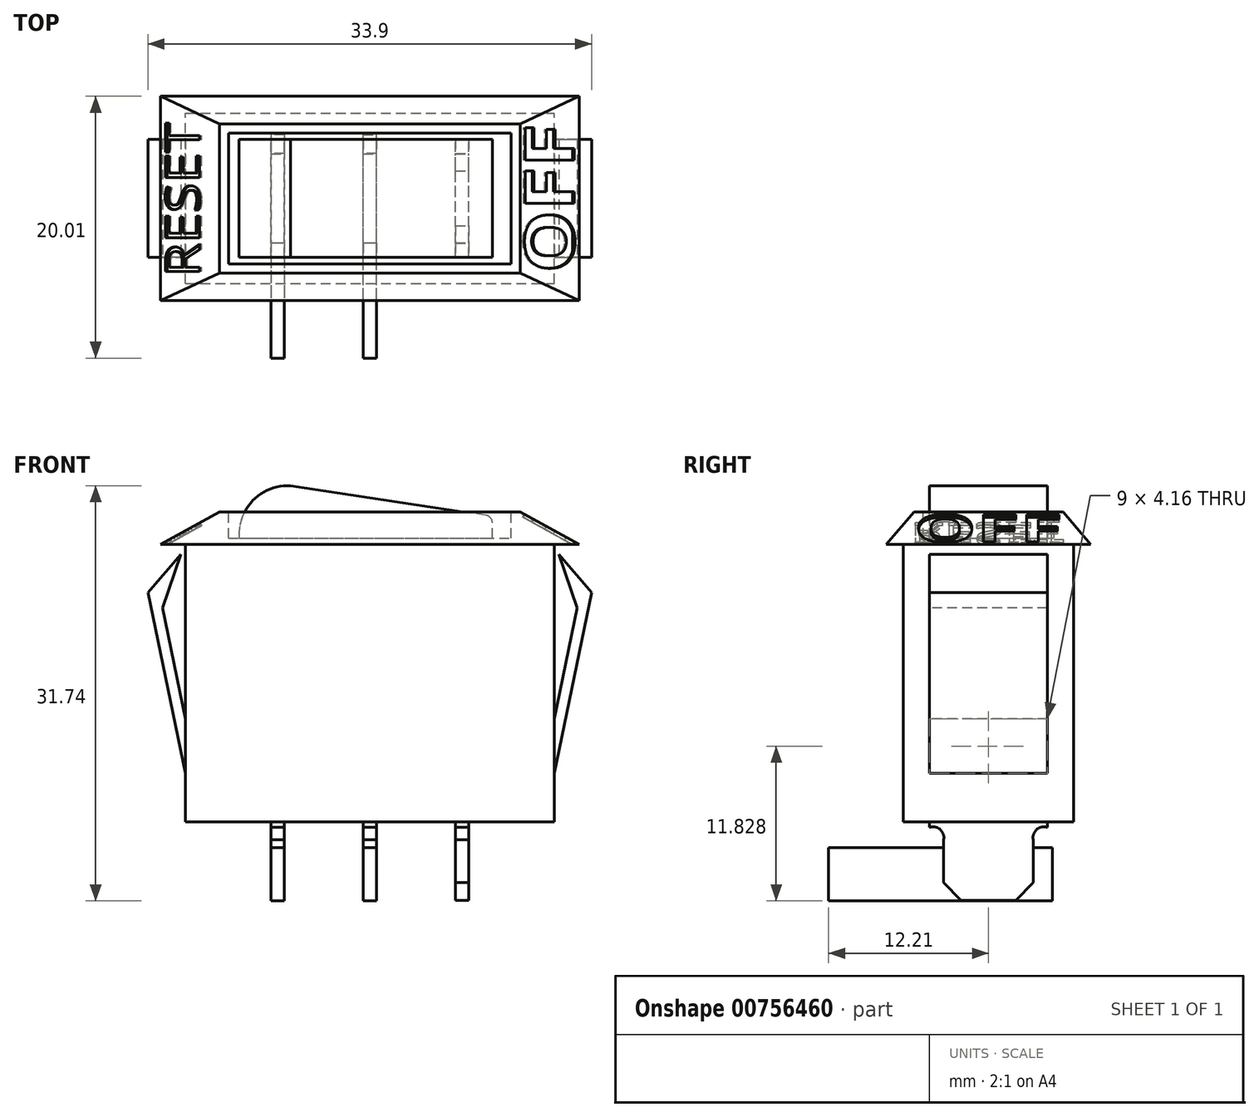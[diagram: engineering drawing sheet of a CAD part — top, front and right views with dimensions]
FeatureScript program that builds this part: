
annotation { "Feature Type Name" : "Feature", "Feature Type Description" : "" }
export const myFeature = defineFeature(function(context is Context, id is Id, definition is map)
    precondition{}
    {
        {
            var Q0;
            Q0=qCreatedBy(makeId("Front.planeOp"),FACE);
            var sketch = newSketch(context, id + "F0", { "sketchPlane" : qUnion([Q0])});
            skLineSegment(sketch, "E0.bottom", {"start": v(-14.1, -10.6) * mm, "end": v(14.1, -10.6) * mm});
            skLineSegment(sketch, "E0.top", {"start": v(-14.1, 10.6) * mm, "end": v(14.1, 10.6) * mm});
            skLineSegment(sketch, "E0.left", {"start": v(-14.1, -10.6) * mm, "end": v(-14.1, 10.6) * mm});
            skLineSegment(sketch, "E0.right", {"start": v(14.1, -10.6) * mm, "end": v(14.1, 10.6) * mm});
            skPoint(sketch, "E0.middle", {"position": v(0, 0) * mm});
            skSolve(sketch);
        }
        {
            var Q0;
            Q0=makeQuery(id+"F0.imprint","IMPRINT",FACE,{"disambiguationData":[TD([[makeQuery(id+"F0.imprint","IMPRINT",EDGE,{"derivedFrom":sQuery(id+"F0.wireOp",EDGE,"E0.bottom")}),1.0]])]});
            extrude(context, id + "F1", {"entities" : qUnion([Q0]), "depth" : 13 * mm, "offsetDistance" : 25 * mm, "symmetric" : true});
        }
        {
            var Q0;
            Q0=makeQuery(id+"F1.opExtrude","SWEPT_FACE",FACE,{"disambiguationData":[OSD([sQuery(id+"F0.wireOp",EDGE,"E0.top")])]});
            var sketch = newSketch(context, id + "F2", { "sketchPlane" : qUnion([Q0])});
            skLineSegment(sketch, "E1.bottom", {"start": v(-16, -7.8) * mm, "end": v(16, -7.8) * mm});
            skLineSegment(sketch, "E1.top", {"start": v(-16, 7.8) * mm, "end": v(16, 7.8) * mm});
            skLineSegment(sketch, "E1.left", {"start": v(-16, -7.8) * mm, "end": v(-16, 7.8) * mm});
            skLineSegment(sketch, "E1.right", {"start": v(16, -7.8) * mm, "end": v(16, 7.8) * mm});
            skPoint(sketch, "E1.middle", {"position": v(0, 0) * mm});
            skSolve(sketch);
        }
        {
            var Q0;
            Q0=makeQuery(id+"F2.imprint","IMPRINT",FACE,{"disambiguationData":[TD([[makeQuery(id+"F2.imprint","IMPRINT",EDGE,{"derivedFrom":sQuery(id+"F2.wireOp",EDGE,"E1.bottom")}),1.0]])]});
            var Q1;
            {var subQ0=sQuery(id+"F0.wireOp",EDGE,"E0.top");Q1=makeQuery(id+"F2.imprint","IMPRINT",FACE,{"disambiguationData":[TD([[makeQuery(id+"F2.imprint","IMPRINT",EDGE,{"derivedFrom":makeQuery(id+"F1.opExtrude","CAP_EDGE",EDGE,{"disambiguationData":[OSD([subQ0])],"isStart":true})}),-1.0]])]});}
            extrude(context, id + "F3", {"entities" : qUnion([Q0, Q1]), "operationType" : NewBodyOperationType.ADD, "depth" : 2.5 * mm, "offsetDistance" : 25 * mm});
        }
        {
            var Q0;
            Q0=makeQuery(id+"F3.opExtrude","CAP_FACE",FACE,{"disambiguationData":[OSD([sQuery(id+"F2.wireOp",EDGE,"E1.bottom"),sQuery(id+"F2.wireOp",EDGE,"E1.top"),sQuery(id+"F2.wireOp",EDGE,"E1.left"),sQuery(id+"F2.wireOp",EDGE,"E1.right")])],"isStart":false});
            var sketch = newSketch(context, id + "F4", { "sketchPlane" : qUnion([Q0])});
            skLineSegment(sketch, "E2.bottom", {"start": v(-10.8, -5) * mm, "end": v(10.8, -5) * mm});
            skLineSegment(sketch, "E2.top", {"start": v(-10.8, 5) * mm, "end": v(10.8, 5) * mm});
            skLineSegment(sketch, "E2.left", {"start": v(-10.8, -5) * mm, "end": v(-10.8, 5) * mm});
            skLineSegment(sketch, "E2.right", {"start": v(10.8, -5) * mm, "end": v(10.8, 5) * mm});
            skPoint(sketch, "E2.middle", {"position": v(0, 0) * mm});
            skSolve(sketch);
        }
        {
            var Q0;
            Q0=makeQuery(id+"F4.imprint","IMPRINT",FACE,{"disambiguationData":[TD([[makeQuery(id+"F4.imprint","IMPRINT",EDGE,{"derivedFrom":sQuery(id+"F4.wireOp",EDGE,"E2.bottom")}),1.0]])]});
            extrude(context, id + "F5", {"entities" : qUnion([Q0]), "operationType" : NewBodyOperationType.REMOVE, "oppositeDirection" : true, "depth" : 2 * mm, "offsetDistance" : 25 * mm});
        }
        {
            var Q0;
            Q0=makeQuery(id+"F5.boolean.opBoolean","COPY",FACE,{"derivedFrom":makeQuery(id+"F5.opExtrude","SWEPT_FACE",FACE,{"disambiguationData":[OSD([sQuery(id+"F4.wireOp",EDGE,"E2.top")])]})});
            cPlane(context, id + "F6", {"entities" : qUnion([Q0]), "cplaneType" : CPlaneType.OFFSET, "offset" : .5 * mm, "width" : 150 * mm, "height" : 150 * mm});
        }
        {
            var Q0;
            Q0=qCreatedBy(id+"F6.planeOp",FACE);
            var sketch = newSketch(context, id + "F7", { "sketchPlane" : qUnion([Q0])});
            skLineSegment(sketch, "E3.0", {"start": v(-10.8, 11.1) * mm, "end": v(10.8, 11.1) * mm});
            skLineSegment(sketch, "E4", {"start": v(-6.06, 11.1) * mm, "end": v(-6.06, 15.1) * mm, "construction": true});
            skArc(sketch, "E5", {"start": v(-6.06, 15.1) * mm, "mid": v(-8.92, 13.98) * mm, "end": v(-10, 11.1) * mm});
            skLineSegment(sketch, "E6", {"start": v(9.36, 11.1) * mm, "end": v(9.36, 12.27) * mm});
            skLineSegment(sketch, "E7", {"start": v(8.88, 12.83) * mm, "end": v(-6.06, 15.1) * mm});
            skPoint(sketch, "E8.visualSharp", {"position": v(9.36, 12.76) * mm});
            skArc(sketch, "E8.filletArc", {"start": v(9.36, 12.27) * mm, "mid": v(9.23, 12.64) * mm, "end": v(8.88, 12.83) * mm});
            skSolve(sketch);
        }
        {
            var Q0;
            {var subQ1=sQuery(id+"F7.wireOp",EDGE,"E5");Q0=makeQuery(id+"F7.imprint","IMPRINT",FACE,{"disambiguationData":[TD([[makeQuery(id+"F7.imprint","IMPRINT",EDGE,{"derivedFrom":subQ1}),1.0]])]});}
            extrude(context, id + "F8", {"entities" : qUnion([Q0]), "operationType" : NewBodyOperationType.ADD, "depth" : 9 * mm, "offsetDistance" : 25 * mm});
        }
        {
            var Q0;
            Q0=makeQuery(id+"F3.opExtrude","SWEPT_FACE",FACE,{"disambiguationData":[OSD([sQuery(id+"F2.wireOp",EDGE,"E1.right")])]});
            var sketch = newSketch(context, id + "F9", { "sketchPlane" : qUnion([Q0])});
            skLineSegment(sketch, "E9.0", {"start": v(-7.8, 13.1) * mm, "end": v(-7.8, 10.6) * mm});
            skLineSegment(sketch, "E9.1", {"start": v(-7.8, 13.1) * mm, "end": v(7.8, 13.1) * mm});
            skLineSegment(sketch, "E9.2", {"start": v(7.8, 13.1) * mm, "end": v(7.8, 10.6) * mm});
            skLineSegment(sketch, "E10", {"start": v(-7.8, 10.6) * mm, "end": v(-5.7, 13.1) * mm});
            skLineSegment(sketch, "E11.0", {"start": v(-5, 11.1) * mm, "end": v(-5, 13.1) * mm, "construction": true});
            skLineSegment(sketch, "E12", {"start": v(0, 10.6) * mm, "end": v(0, 13.1) * mm, "construction": true});
            skLineSegment(sketch, "E13.MirrorCS", {"start": v(7.8, 10.6) * mm, "end": v(5.7, 13.1) * mm});
            skSolve(sketch);
        }
        {
            var Q0;
            {var subQ0=sQuery(id+"F9.wireOp",EDGE,"E9.0");Q0=makeQuery(id+"F9.imprint","IMPRINT",FACE,{"disambiguationData":[TD([[makeQuery(id+"F9.imprint","IMPRINT",EDGE,{"derivedFrom":subQ0}),1.0]])]});}
            var Q1;
            {var subQ0=sQuery(id+"F9.wireOp",EDGE,"E9.2");Q1=makeQuery(id+"F9.imprint","IMPRINT",FACE,{"disambiguationData":[TD([[makeQuery(id+"F9.imprint","IMPRINT",EDGE,{"derivedFrom":subQ0}),-1.0]])]});}
            extrude(context, id + "F10", {"entities" : qUnion([Q0, Q1]), "operationType" : NewBodyOperationType.REMOVE, "endBound" : BoundingType.THROUGH_ALL, "oppositeDirection" : true, "depth" : 25 * mm, "offsetDistance" : 25 * mm});
        }
        {
            var Q0;
            Q0=makeQuery(id+"F1.opExtrude","CAP_FACE",FACE,{"disambiguationData":[OSD([sQuery(id+"F0.wireOp",EDGE,"E0.bottom"),sQuery(id+"F0.wireOp",EDGE,"E0.top"),sQuery(id+"F0.wireOp",EDGE,"E0.left"),sQuery(id+"F0.wireOp",EDGE,"E0.right")])],"isStart":false});
            cPlane(context, id + "F11", {"entities" : qUnion([Q0]), "cplaneType" : CPlaneType.OFFSET, "offset" : 1.3 * mm, "width" : 150 * mm, "height" : 150 * mm});
        }
        {
            var Q0;
            Q0=qCreatedBy(id+"F11.planeOp",FACE);
            var sketch = newSketch(context, id + "F12", { "sketchPlane" : qUnion([Q0])});
            skLineSegment(sketch, "E14.0", {"start": v(-16, 13.1) * mm, "end": v(-16, 10.6) * mm});
            skLineSegment(sketch, "E14.1", {"start": v(-16, 13.1) * mm, "end": v(16, 13.1) * mm});
            skLineSegment(sketch, "E14.2", {"start": v(16, 10.6) * mm, "end": v(16, 13.1) * mm});
            skLineSegment(sketch, "E15.0", {"start": v(-10.8, 11.1) * mm, "end": v(-10.8, 13.1) * mm, "construction": true});
            skLineSegment(sketch, "E16", {"start": v(0, 13.1) * mm, "end": v(0, 10.69) * mm, "construction": true});
            skLineSegment(sketch, "E17", {"start": v(-16, 10.6) * mm, "end": v(-11.5, 13.1) * mm});
            skLineSegment(sketch, "E18.MirrorCS", {"start": v(16, 10.6) * mm, "end": v(11.5, 13.1) * mm});
            skSolve(sketch);
        }
        {
            var Q0;
            {var subQ0=sQuery(id+"F12.wireOp",EDGE,"E14.0");Q0=makeQuery(id+"F12.imprint","IMPRINT",FACE,{"disambiguationData":[TD([[makeQuery(id+"F12.imprint","IMPRINT",EDGE,{"derivedFrom":subQ0}),1.0]])]});}
            var Q1;
            {var subQ0=sQuery(id+"F12.wireOp",EDGE,"E14.2");Q1=makeQuery(id+"F12.imprint","IMPRINT",FACE,{"disambiguationData":[TD([[makeQuery(id+"F12.imprint","IMPRINT",EDGE,{"derivedFrom":subQ0}),1.0]])]});}
            extrude(context, id + "F13", {"entities" : qUnion([Q0, Q1]), "operationType" : NewBodyOperationType.REMOVE, "endBound" : BoundingType.THROUGH_ALL, "oppositeDirection" : true, "depth" : 25 * mm, "offsetDistance" : 25 * mm});
        }
        {
            var Q0;
            Q0=makeQuery(id+"F1.opExtrude","CAP_FACE",FACE,{"disambiguationData":[OSD([sQuery(id+"F0.wireOp",EDGE,"E0.bottom"),sQuery(id+"F0.wireOp",EDGE,"E0.top"),sQuery(id+"F0.wireOp",EDGE,"E0.left"),sQuery(id+"F0.wireOp",EDGE,"E0.right")])],"isStart":false});
            cPlane(context, id + "F14", {"entities" : qUnion([Q0]), "cplaneType" : CPlaneType.OFFSET, "offset" : 2 * mm, "oppositeDirection" : true, "width" : 150 * mm, "height" : 150 * mm});
        }
        {
            var Q0;
            Q0=qCreatedBy(id+"F14.planeOp",FACE);
            var sketch = newSketch(context, id + "F15", { "sketchPlane" : qUnion([Q0])});
            skLineSegment(sketch, "E19.0", {"start": v(-14.1, -10.6) * mm, "end": v(-14.1, 10.6) * mm});
            skLineSegment(sketch, "E19.1", {"start": v(14.1, -10.6) * mm, "end": v(14.1, 10.6) * mm});
            skLineSegment(sketch, "E20", {"start": v(-14.1, -6.9) * mm, "end": v(-16.95, 6.94) * mm});
            skLineSegment(sketch, "E21", {"start": v(-16.95, 6.94) * mm, "end": v(-14.45, 9.87) * mm});
            skLineSegment(sketch, "E22", {"start": v(-14.45, 9.87) * mm, "end": v(-15.85, 5.76) * mm});
            skLineSegment(sketch, "E23", {"start": v(-15.85, 5.76) * mm, "end": v(-14.1, -2.73) * mm});
            skLineSegment(sketch, "E24", {"start": v(0, -10.46) * mm, "end": v(0, 10.68) * mm, "construction": true});
            skLineSegment(sketch, "E25.MirrorCS", {"start": v(15.85, 5.76) * mm, "end": v(14.1, -2.73) * mm});
            skLineSegment(sketch, "E26.MirrorCS", {"start": v(14.1, -6.9) * mm, "end": v(16.95, 6.94) * mm});
            skLineSegment(sketch, "E27.MirrorCS", {"start": v(14.45, 9.87) * mm, "end": v(15.85, 5.76) * mm});
            skLineSegment(sketch, "E28.MirrorCS", {"start": v(16.95, 6.94) * mm, "end": v(14.45, 9.87) * mm});
            skSolve(sketch);
        }
        {
            var Q0;
            {var subQ0=sQuery(id+"F15.wireOp",EDGE,"E20");Q0=makeQuery(id+"F15.imprint","IMPRINT",FACE,{"disambiguationData":[TD([[makeQuery(id+"F15.imprint","IMPRINT",EDGE,{"derivedFrom":subQ0}),-1.0]])]});}
            var Q1;
            {var subQ1=sQuery(id+"F15.wireOp",EDGE,"E25.MirrorCS");Q1=makeQuery(id+"F15.imprint","IMPRINT",FACE,{"disambiguationData":[TD([[makeQuery(id+"F15.imprint","IMPRINT",EDGE,{"derivedFrom":subQ1}),1.0]])]});}
            extrude(context, id + "F16", {"entities" : qUnion([Q0, Q1]), "operationType" : NewBodyOperationType.ADD, "oppositeDirection" : true, "depth" : 9 * mm, "offsetDistance" : 25 * mm});
        }
        {
            var Q0;
            Q0=makeQuery(id+"F1.opExtrude","SWEPT_FACE",FACE,{"disambiguationData":[OSD([sQuery(id+"F0.wireOp",EDGE,"E0.bottom")])]});
            var sketch = newSketch(context, id + "F17", { "sketchPlane" : qUnion([Q0])});
            skLineSegment(sketch, "E29", {"start": v(-14.1, 0) * mm, "end": v(14.1, 0) * mm, "construction": true});
            skLineSegment(sketch, "E30", {"start": v(0, 6.5) * mm, "end": v(0, -6.5) * mm, "construction": true});
            skLineSegment(sketch, "E31", {"start": v(-7.05, 6.5) * mm, "end": v(-7.05, -6.5) * mm, "construction": true});
            skLineSegment(sketch, "E32.MirrorCS", {"start": v(7.05, 6.5) * mm, "end": v(7.05, -6.5) * mm, "construction": true});
            skPoint(sketch, "E33", {"position": v(-7.05, 0) * mm});
            skPoint(sketch, "E34", {"position": v(7.05, 0) * mm});
            skPoint(sketch, "E35", {"position": v(0, 0) * mm});
            skLineSegment(sketch, "E36.bottom", {"start": v(-7.55, 4.5) * mm, "end": v(-6.55, 4.5) * mm});
            skLineSegment(sketch, "E36.top", {"start": v(-7.55, -4.5) * mm, "end": v(-6.55, -4.5) * mm});
            skLineSegment(sketch, "E36.left", {"start": v(-7.55, 4.5) * mm, "end": v(-7.55, -4.5) * mm});
            skLineSegment(sketch, "E36.right", {"start": v(-6.55, 4.5) * mm, "end": v(-6.55, -4.5) * mm});
            skLineSegment(sketch, "E37.bottom", {"start": v(-0.5, 4.5) * mm, "end": v(0.5, 4.5) * mm});
            skLineSegment(sketch, "E37.top", {"start": v(-0.5, -4.5) * mm, "end": v(0.5, -4.5) * mm});
            skLineSegment(sketch, "E37.left", {"start": v(-0.5, 4.5) * mm, "end": v(-0.5, -4.5) * mm});
            skLineSegment(sketch, "E37.right", {"start": v(0.5, 4.5) * mm, "end": v(0.5, -4.5) * mm});
            skLineSegment(sketch, "E38.bottom", {"start": v(6.55, 4.5) * mm, "end": v(7.55, 4.5) * mm});
            skLineSegment(sketch, "E38.top", {"start": v(6.55, -4.5) * mm, "end": v(7.55, -4.5) * mm});
            skLineSegment(sketch, "E38.left", {"start": v(6.55, 4.5) * mm, "end": v(6.55, -4.5) * mm});
            skLineSegment(sketch, "E38.right", {"start": v(7.55, 4.5) * mm, "end": v(7.55, -4.5) * mm});
            skSolve(sketch);
        }
        {
            var Q0;
            Q0=makeQuery(id+"F17.imprint","IMPRINT",FACE,{"disambiguationData":[TD([[makeQuery(id+"F17.imprint","IMPRINT",EDGE,{"derivedFrom":sQuery(id+"F17.wireOp",EDGE,"E36.bottom")}),-1.0]])]});
            var Q1;
            Q1=makeQuery(id+"F17.imprint","IMPRINT",FACE,{"disambiguationData":[TD([[makeQuery(id+"F17.imprint","IMPRINT",EDGE,{"derivedFrom":sQuery(id+"F17.wireOp",EDGE,"E37.bottom")}),-1.0]])]});
            var Q2;
            Q2=makeQuery(id+"F17.imprint","IMPRINT",FACE,{"disambiguationData":[TD([[makeQuery(id+"F17.imprint","IMPRINT",EDGE,{"derivedFrom":sQuery(id+"F17.wireOp",EDGE,"E38.bottom")}),-1.0]])]});
            extrude(context, id + "F18", {"entities" : qUnion([Q0, Q1, Q2]), "operationType" : NewBodyOperationType.ADD, "depth" : 6 * mm, "offsetDistance" : 25 * mm});
        }
        {
            var Q0;
            Q0=makeQuery(id+"F18.opExtrude","SWEPT_FACE",FACE,{"disambiguationData":[OSD([sQuery(id+"F17.wireOp",EDGE,"E38.right")])]});
            var sketch = newSketch(context, id + "F19", { "sketchPlane" : qUnion([Q0])});
            skLineSegment(sketch, "E39.0", {"start": v(-4.5, -16.6) * mm, "end": v(-4.5, -10.6) * mm});
            skLineSegment(sketch, "E39.1", {"start": v(4.5, -16.6) * mm, "end": v(4.5, -10.6) * mm});
            skLineSegment(sketch, "E39.2", {"start": v(-4.5, -16.6) * mm, "end": v(4.5, -16.6) * mm});
            skLineSegment(sketch, "E40.0", {"start": v(-6.5, -10.6) * mm, "end": v(6.5, -10.6) * mm});
            skLineSegment(sketch, "E41", {"start": v(0, -16.6) * mm, "end": v(0, -10.6) * mm, "construction": true});
            skLineSegment(sketch, "E42", {"start": v(-2.1, -16.6) * mm, "end": v(-3.42, -15.23) * mm});
            skLineSegment(sketch, "E43", {"start": v(-3.42, -15.23) * mm, "end": v(-3.42, -11.97) * mm});
            skArc(sketch, "E44", {"start": v(-3.42, -11.97) * mm, "mid": v(-3.69, -11.18) * mm, "end": v(-4.5, -11.02) * mm});
            skLineSegment(sketch, "E45.MirrorCS", {"start": v(2.1, -16.6) * mm, "end": v(3.42, -15.23) * mm});
            skLineSegment(sketch, "E46.MirrorCS", {"start": v(3.42, -15.23) * mm, "end": v(3.42, -11.97) * mm});
            skArc(sketch, "E47.MirrorCS", {"start": v(3.42, -11.97) * mm, "mid": v(3.69, -11.18) * mm, "end": v(4.5, -11.02) * mm});
            skSolve(sketch);
        }
        {
            var Q0;
            {var subQ0=sQuery(id+"F19.wireOp",EDGE,"E42");Q0=makeQuery(id+"F19.imprint","IMPRINT",FACE,{"disambiguationData":[TD([[makeQuery(id+"F19.imprint","IMPRINT",EDGE,{"derivedFrom":subQ0}),1.0]])]});}
            var Q1;
            {var subQ0=sQuery(id+"F19.wireOp",EDGE,"E45.MirrorCS");Q1=makeQuery(id+"F19.imprint","IMPRINT",FACE,{"disambiguationData":[TD([[makeQuery(id+"F19.imprint","IMPRINT",EDGE,{"derivedFrom":subQ0}),-1.0]])]});}
            extrude(context, id + "F20", {"entities" : qUnion([Q0, Q1]), "operationType" : NewBodyOperationType.REMOVE, "endBound" : BoundingType.THROUGH_ALL, "oppositeDirection" : true, "depth" : 25 * mm, "offsetDistance" : 25 * mm});
        }
        {
            var Q0;
            Q0=makeQuery(id+"F18.opExtrude","SWEPT_FACE",FACE,{"disambiguationData":[OSD([sQuery(id+"F17.wireOp",EDGE,"E37.right")])]});
            var sketch = newSketch(context, id + "F21", { "sketchPlane" : qUnion([Q0])});
            skLineSegment(sketch, "E48.bottom", {"start": v(-4.87, -16.64) * mm, "end": v(4.87, -16.64) * mm});
            skLineSegment(sketch, "E48.top", {"start": v(-4.87, -12.55) * mm, "end": v(4.87, -12.55) * mm});
            skLineSegment(sketch, "E48.right", {"start": v(4.87, -16.64) * mm, "end": v(4.87, -12.55) * mm});
            skPoint(sketch, "E48.middle", {"position": v(0, -14.6) * mm});
            skLineSegment(sketch, "E49", {"start": v(-4.87, -12.55) * mm, "end": v(-12.21, -12.55) * mm});
            skLineSegment(sketch, "E50", {"start": v(-12.21, -12.55) * mm, "end": v(-12.21, -16.64) * mm});
            skLineSegment(sketch, "E51", {"start": v(-12.21, -16.64) * mm, "end": v(-4.87, -16.64) * mm});
            skSolve(sketch);
        }
        {
            var Q0;
            Q0 = qSketchRegion(id + "F21", true);
            extrude(context, id + "F22", {"entities" : qUnion([Q0]), "operationType" : NewBodyOperationType.ADD, "oppositeDirection" : true, "depth" : 1 * mm, "offsetDistance" : 25 * mm});
        }
        {
            var Q0;
            Q0=makeQuery(id+"F18.opExtrude","SWEPT_FACE",FACE,{"disambiguationData":[OSD([sQuery(id+"F17.wireOp",EDGE,"E36.left")])]});
            var sketch = newSketch(context, id + "F23", { "sketchPlane" : qUnion([Q0])});
            skPoint(sketch, "E52.0", {"position": v(-4.87, -12.55) * mm});
            skPoint(sketch, "E52.1", {"position": v(-4.87, -16.64) * mm});
            skPoint(sketch, "E52.2", {"position": v(12.21, -16.64) * mm});
            skPoint(sketch, "E52.3", {"position": v(12.21, -12.55) * mm});
            skLineSegment(sketch, "E53.bottom", {"start": v(-4.87, -12.55) * mm, "end": v(12.21, -12.55) * mm});
            skLineSegment(sketch, "E53.top", {"start": v(-4.87, -16.64) * mm, "end": v(12.21, -16.64) * mm});
            skLineSegment(sketch, "E53.left", {"start": v(-4.87, -12.55) * mm, "end": v(-4.87, -16.64) * mm});
            skLineSegment(sketch, "E53.right", {"start": v(12.21, -12.55) * mm, "end": v(12.21, -16.64) * mm});
            skSolve(sketch);
        }
        {
            var Q0;
            Q0=makeQuery(id+"F23.imprint","IMPRINT",FACE,{"disambiguationData":[TD([[makeQuery(id+"F23.imprint","IMPRINT",EDGE,{"derivedFrom":sQuery(id+"F23.wireOp",EDGE,"E53.top")}),1.0]])]});
            extrude(context, id + "F24", {"entities" : qUnion([Q0]), "operationType" : NewBodyOperationType.ADD, "oppositeDirection" : true, "depth" : 1 * mm, "offsetDistance" : 25 * mm});
        }
        {
            var Q0;
            Q0=makeQuery(id+"F13.boolean.opBoolean","COPY",FACE,{"derivedFrom":makeQuery(id+"F13.opExtrude","SWEPT_FACE",FACE,{"disambiguationData":[OSD([sQuery(id+"F12.wireOp",EDGE,"E18.MirrorCS")])]})});
            var sketch = newSketch(context, id + "F25", { "sketchPlane" : qUnion([Q0])});
            skText(sketch, "E54", { "text": "OFF", "fontName": "OpenSans-Bold.ttf"});
            const initialGuessF25  = {"E54": [0.00842, -0.0057, 0, 1, 0.00433]};
            skSetInitialGuess(sketch, initialGuessF25);
            skSolve(sketch);
        }
        {
            var Q0;
            Q0=makeQuery(id+"F25.imprint","IMPRINT",FACE,{"disambiguationData":[TD([[makeQuery(id+"F25.imprint","IMPRINT",EDGE,{"derivedFrom":sQuery(id+"F25.wireOp",EDGE,"E54.sketch_text.stroke-0")}),-1.0]])]});
            var Q1;
            Q1=makeQuery(id+"F25.imprint","IMPRINT",FACE,{"disambiguationData":[TD([[makeQuery(id+"F25.imprint","IMPRINT",EDGE,{"derivedFrom":sQuery(id+"F25.wireOp",EDGE,"E54.sketch_text.stroke-14")}),-1.0]])]});
            var Q2;
            Q2=makeQuery(id+"F25.imprint","IMPRINT",FACE,{"disambiguationData":[TD([[makeQuery(id+"F25.imprint","IMPRINT",EDGE,{"derivedFrom":sQuery(id+"F25.wireOp",EDGE,"E54.sketch_text.stroke-24")}),-1.0]])]});
            extrude(context, id + "F26", {"entities" : qUnion([Q0, Q1, Q2]), "operationType" : NewBodyOperationType.REMOVE, "oppositeDirection" : true, "depth" : .25 * mm, "offsetDistance" : 25 * mm});
        }
        {
            var Q0;
            Q0=makeQuery(id+"F13.boolean.opBoolean","COPY",FACE,{"derivedFrom":makeQuery(id+"F13.opExtrude","SWEPT_FACE",FACE,{"disambiguationData":[OSD([sQuery(id+"F12.wireOp",EDGE,"E17")])]})});
            var sketch = newSketch(context, id + "F27", { "sketchPlane" : qUnion([Q0])});
            skText(sketch, "E55", { "text": "RESET", "fontName": "OpenSans-Regular.ttf"});
            const initialGuessF27  = {"E55": [-0.00542, -0.00601, 0, 1, 0.003]};
            skSetInitialGuess(sketch, initialGuessF27);
            skSolve(sketch);
        }
        {
            var Q0;
            Q0 = qSketchRegion(id + "F27", true);
            extrude(context, id + "F28", {"entities" : qUnion([Q0]), "operationType" : NewBodyOperationType.REMOVE, "oppositeDirection" : true, "depth" : .25 * mm, "offsetDistance" : 25 * mm});
        }
    });
